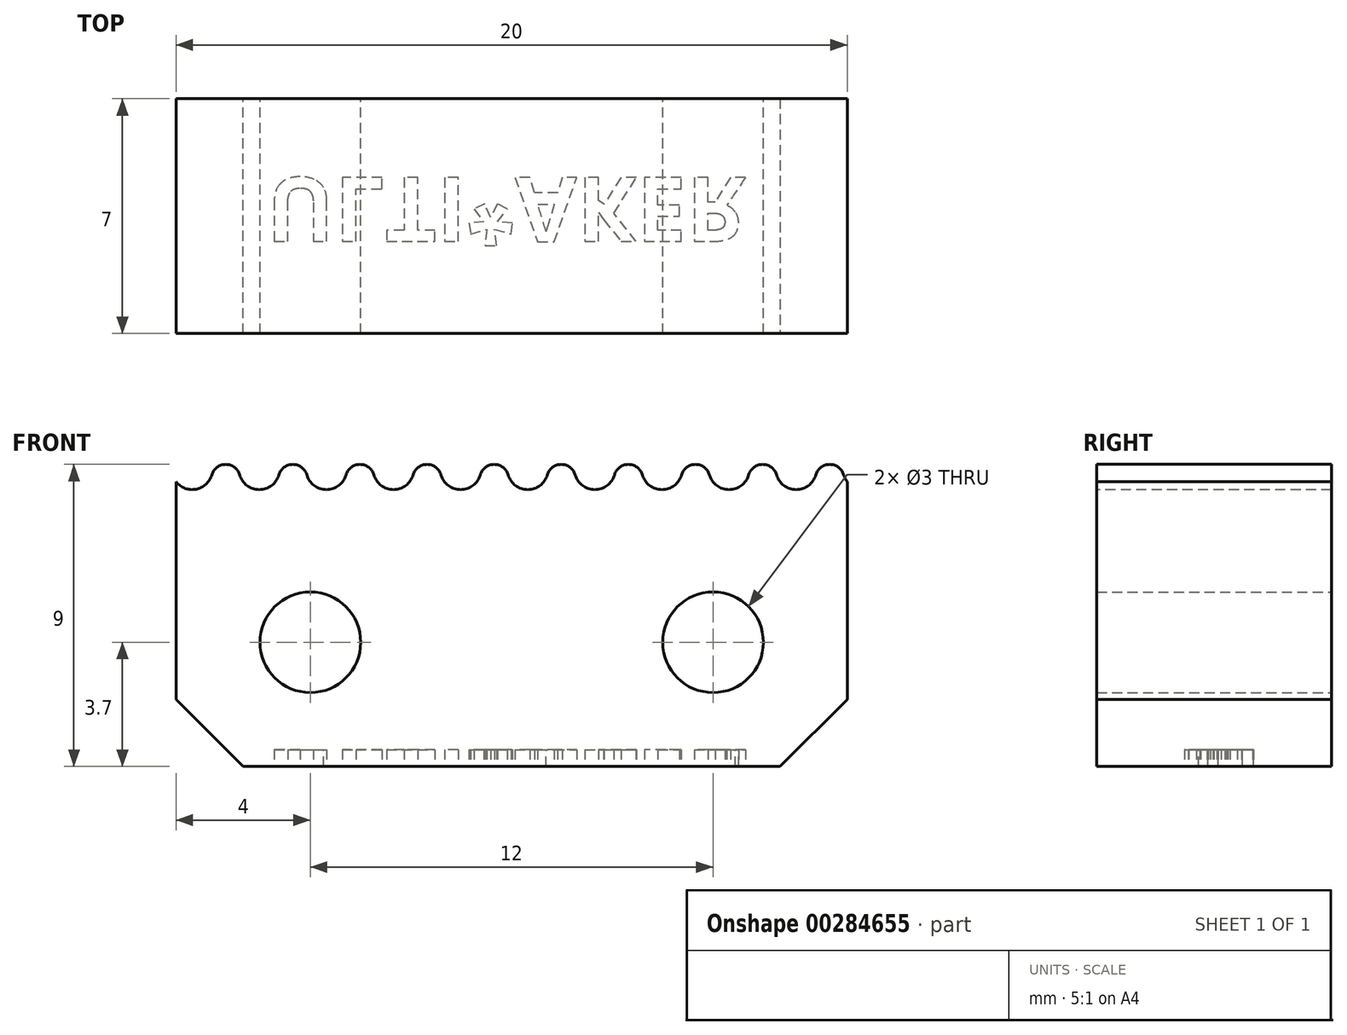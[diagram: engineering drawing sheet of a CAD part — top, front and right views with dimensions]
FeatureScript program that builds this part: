
annotation { "Feature Type Name" : "Feature", "Feature Type Description" : "" }
export const myFeature = defineFeature(function(context is Context, id is Id, definition is map)
    precondition{}
    {
        {
            var Q0;
            Q0=qCreatedBy(makeId("Front.planeOp"),FACE);
            var sketch = newSketch(context, id + "F0", { "sketchPlane" : qUnion([Q0])});
            skLineSegment(sketch, "E0.bottom", {"start": v(2, 1) * mm, "end": v(22, 1) * mm});
            skLineSegment(sketch, "E0.top", {"start": v(2, 10) * mm, "end": v(22, 10) * mm});
            skLineSegment(sketch, "E0.left", {"start": v(2, 1) * mm, "end": v(2, 10) * mm});
            skLineSegment(sketch, "E0.right", {"start": v(22, 1) * mm, "end": v(22, 10) * mm});
            skCircle(sketch, "E1", {"center": v(6, 4.7) * mm, "radius": 1.5 * mm});
            skPoint(sketch, "E1.centerSnap0", {"position": v(2, 4.7) * mm});
            skCircle(sketch, "E2", {"center": v(18, 4.7) * mm, "radius": 1.5 * mm});
            skPoint(sketch, "E2.centerSnap0", {"position": v(22, 4.7) * mm});
            skSolve(sketch);
        }
        {
            var Q0;
            Q0=makeQuery(id+"F0.imprint","IMPRINT",FACE,{"disambiguationData":[TD([[makeQuery(id+"F0.imprint","IMPRINT",EDGE,{"derivedFrom":sQuery(id+"F0.wireOp",EDGE,"E0.bottom")}),1.0]])]});
            extrude(context, id + "F1", {"entities" : qUnion([Q0]), "depth" : 7 * mm});
        }
        {
            var Q0;
            Q0=makeQuery(id+"F1.opExtrude","CAP_FACE",FACE,{"disambiguationData":[OSD([sQuery(id+"F0.wireOp",EDGE,"E0.bottom"),sQuery(id+"F0.wireOp",EDGE,"E0.top"),sQuery(id+"F0.wireOp",EDGE,"E0.left"),sQuery(id+"F0.wireOp",EDGE,"E0.right"),sQuery(id+"F0.wireOp",EDGE,"E1"),sQuery(id+"F0.wireOp",EDGE,"E2")])],"isStart":false});
            var sketch = newSketch(context, id + "F2", { "sketchPlane" : qUnion([Q0])});
            skLineSegment(sketch, "E3.top", {"start": v(0, 10.63) * mm, "end": v(22.94, 10.63) * mm});
            skArc(sketch, "E4", {"start": v(2.48, 9.25) * mm, "mid": v(2.84, 9.37) * mm, "end": v(3.06, 9.69) * mm});
            skArc(sketch, "E5", {"start": v(3.9, 9.69) * mm, "mid": v(4.11, 9.37) * mm, "end": v(4.48, 9.25) * mm});
            skArc(sketch, "E6", {"start": v(3.9, 9.69) * mm, "mid": v(3.48, 10) * mm, "end": v(3.06, 9.69) * mm});
            skPoint(sketch, "E6.first.point", {"position": v(3.48, 10) * mm});
            skPoint(sketch, "E6.second.point", {"position": v(3.06, 9.69) * mm});
            skPoint(sketch, "E6.third.point", {"position": v(3.9, 9.69) * mm});
            skLineSegment(sketch, "E7.trimOffspring", {"start": v(3.48, 10) * mm, "end": v(3.48, 10) * mm});
            skLineSegment(sketch, "E8", {"start": v(4.48, 10.86) * mm, "end": v(4.48, 10.63) * mm});
            skPoint(sketch, "E9.start.orphan", {"position": v(2.48, 10.63) * mm});
            skArc(sketch, "E10.1.0.0", {"start": v(5.9, 9.69) * mm, "mid": v(6.11, 9.37) * mm, "end": v(6.48, 9.25) * mm});
            skPoint(sketch, "E10.1.0.1", {"position": v(5.06, 9.69) * mm});
            skArc(sketch, "E10.1.0.2", {"start": v(4.48, 9.25) * mm, "mid": v(4.84, 9.37) * mm, "end": v(5.06, 9.69) * mm});
            skArc(sketch, "E10.1.0.3", {"start": v(5.9, 9.69) * mm, "mid": v(5.48, 10) * mm, "end": v(5.06, 9.69) * mm});
            skArc(sketch, "E10.2.0.0", {"start": v(7.9, 9.69) * mm, "mid": v(8.11, 9.37) * mm, "end": v(8.48, 9.25) * mm});
            skPoint(sketch, "E10.2.0.1", {"position": v(7.06, 9.69) * mm});
            skArc(sketch, "E10.2.0.2", {"start": v(6.48, 9.25) * mm, "mid": v(6.84, 9.37) * mm, "end": v(7.06, 9.69) * mm});
            skArc(sketch, "E10.2.0.3", {"start": v(7.9, 9.69) * mm, "mid": v(7.48, 10) * mm, "end": v(7.06, 9.69) * mm});
            skArc(sketch, "E10.3.0.0", {"start": v(9.9, 9.69) * mm, "mid": v(10.11, 9.37) * mm, "end": v(10.48, 9.25) * mm});
            skPoint(sketch, "E10.3.0.1", {"position": v(9.06, 9.69) * mm});
            skArc(sketch, "E10.3.0.2", {"start": v(8.48, 9.25) * mm, "mid": v(8.84, 9.37) * mm, "end": v(9.06, 9.69) * mm});
            skArc(sketch, "E10.3.0.3", {"start": v(9.9, 9.69) * mm, "mid": v(9.48, 10) * mm, "end": v(9.06, 9.69) * mm});
            skArc(sketch, "E10.4.0.0", {"start": v(11.9, 9.69) * mm, "mid": v(12.11, 9.37) * mm, "end": v(12.48, 9.25) * mm});
            skPoint(sketch, "E10.4.0.1", {"position": v(11.06, 9.69) * mm});
            skArc(sketch, "E10.4.0.2", {"start": v(10.48, 9.25) * mm, "mid": v(10.84, 9.37) * mm, "end": v(11.06, 9.69) * mm});
            skArc(sketch, "E10.4.0.3", {"start": v(11.9, 9.69) * mm, "mid": v(11.48, 10) * mm, "end": v(11.06, 9.69) * mm});
            skArc(sketch, "E10.5.0.0", {"start": v(13.9, 9.69) * mm, "mid": v(14.11, 9.37) * mm, "end": v(14.48, 9.25) * mm});
            skPoint(sketch, "E10.5.0.1", {"position": v(13.06, 9.69) * mm});
            skArc(sketch, "E10.5.0.2", {"start": v(12.48, 9.25) * mm, "mid": v(12.84, 9.37) * mm, "end": v(13.06, 9.69) * mm});
            skArc(sketch, "E10.5.0.3", {"start": v(13.9, 9.69) * mm, "mid": v(13.48, 10) * mm, "end": v(13.06, 9.69) * mm});
            skArc(sketch, "E10.6.0.0", {"start": v(15.9, 9.69) * mm, "mid": v(16.11, 9.37) * mm, "end": v(16.48, 9.25) * mm});
            skPoint(sketch, "E10.6.0.1", {"position": v(15.06, 9.69) * mm});
            skArc(sketch, "E10.6.0.2", {"start": v(14.48, 9.25) * mm, "mid": v(14.84, 9.37) * mm, "end": v(15.06, 9.69) * mm});
            skArc(sketch, "E10.6.0.3", {"start": v(15.9, 9.69) * mm, "mid": v(15.48, 10) * mm, "end": v(15.06, 9.69) * mm});
            skArc(sketch, "E10.7.0.0", {"start": v(17.9, 9.69) * mm, "mid": v(18.11, 9.37) * mm, "end": v(18.48, 9.25) * mm});
            skPoint(sketch, "E10.7.0.1", {"position": v(17.06, 9.69) * mm});
            skArc(sketch, "E10.7.0.2", {"start": v(16.48, 9.25) * mm, "mid": v(16.84, 9.37) * mm, "end": v(17.06, 9.69) * mm});
            skArc(sketch, "E10.7.0.3", {"start": v(17.9, 9.69) * mm, "mid": v(17.48, 10) * mm, "end": v(17.06, 9.69) * mm});
            skArc(sketch, "E10.8.0.0", {"start": v(19.9, 9.69) * mm, "mid": v(20.11, 9.37) * mm, "end": v(20.48, 9.25) * mm});
            skPoint(sketch, "E10.8.0.1", {"position": v(19.06, 9.69) * mm});
            skArc(sketch, "E10.8.0.2", {"start": v(18.48, 9.25) * mm, "mid": v(18.84, 9.37) * mm, "end": v(19.06, 9.69) * mm});
            skArc(sketch, "E10.8.0.3", {"start": v(19.9, 9.69) * mm, "mid": v(19.48, 10) * mm, "end": v(19.06, 9.69) * mm});
            skArc(sketch, "E10.9.0.0", {"start": v(21.9, 9.69) * mm, "mid": v(22.11, 9.37) * mm, "end": v(22.48, 9.25) * mm});
            skPoint(sketch, "E10.9.0.1", {"position": v(21.06, 9.69) * mm});
            skArc(sketch, "E10.9.0.2", {"start": v(20.48, 9.25) * mm, "mid": v(20.84, 9.37) * mm, "end": v(21.06, 9.69) * mm});
            skArc(sketch, "E10.9.0.3", {"start": v(21.9, 9.69) * mm, "mid": v(21.48, 10) * mm, "end": v(21.06, 9.69) * mm});
            skArc(sketch, "E10.10.0.0", {"start": v(23.9, 9.69) * mm, "mid": v(24.11, 9.37) * mm, "end": v(24.48, 9.25) * mm});
            skPoint(sketch, "E10.10.0.1", {"position": v(23.06, 9.69) * mm});
            skArc(sketch, "E10.10.0.2", {"start": v(22.48, 9.25) * mm, "mid": v(22.84, 9.37) * mm, "end": v(23.06, 9.69) * mm});
            skArc(sketch, "E10.10.0.3", {"start": v(23.9, 9.69) * mm, "mid": v(23.48, 10) * mm, "end": v(23.06, 9.69) * mm});
            skPoint(sketch, "E10.11.0.1", {"position": v(25.06, 9.69) * mm});
            skArc(sketch, "E11.1.0.0", {"start": v(0.48, 9.25) * mm, "mid": v(0.84, 9.37) * mm, "end": v(1.06, 9.69) * mm});
            skArc(sketch, "E11.1.0.1", {"start": v(1.9, 9.69) * mm, "mid": v(1.48, 10) * mm, "end": v(1.06, 9.69) * mm});
            skArc(sketch, "E11.1.0.2", {"start": v(1.9, 9.69) * mm, "mid": v(2.11, 9.37) * mm, "end": v(2.48, 9.25) * mm});
            skArc(sketch, "E11.2.0.0", {"start": v(-1.52, 9.25) * mm, "mid": v(-1.16, 9.37) * mm, "end": v(-0.94, 9.69) * mm});
            skArc(sketch, "E11.2.0.1", {"start": v(-0.1, 9.69) * mm, "mid": v(-0.52, 10) * mm, "end": v(-0.94, 9.69) * mm});
            skArc(sketch, "E11.2.0.2", {"start": v(-0.1, 9.69) * mm, "mid": v(0.11, 9.37) * mm, "end": v(0.48, 9.25) * mm});
            skLineSegment(sketch, "E11.direction1", {"start": v(2.48, 9.25) * mm, "end": v(0.48, 9.25) * mm, "construction": true});
            skLineSegment(sketch, "E12", {"start": v(0, 10.63) * mm, "end": v(-1.66, 10.63) * mm});
            skLineSegment(sketch, "E13", {"start": v(-1.66, 10.63) * mm, "end": v(-1.52, 9.25) * mm});
            skLineSegment(sketch, "E14", {"start": v(22.94, 10.63) * mm, "end": v(24.4, 10.63) * mm});
            skLineSegment(sketch, "E15", {"start": v(24.4, 10.63) * mm, "end": v(24.48, 9.25) * mm});
            skSolve(sketch);
        }
        {
            var Q0;
            Q0=makeQuery(id+"F2.imprint","IMPRINT",FACE,{"disambiguationData":[TD([[makeQuery(id+"F2.imprint","IMPRINT",EDGE,{"derivedFrom":sQuery(id+"F2.wireOp",EDGE,"E11.2.0.0")}),1.0]])]});
            var Q1;
            {var subQ1=sQuery(id+"F2.wireOp",EDGE,"E11.1.0.0");Q1=makeQuery(id+"F2.imprint","IMPRINT",FACE,{"disambiguationData":[TD([[makeQuery(id+"F2.imprint","IMPRINT",EDGE,{"derivedFrom":subQ1}),1.0]])]});}
            var Q2;
            {var subQ5=sQuery(id+"F2.wireOp",EDGE,"E4");Q2=makeQuery(id+"F2.imprint","IMPRINT",FACE,{"disambiguationData":[TD([[makeQuery(id+"F2.imprint","IMPRINT",EDGE,{"derivedFrom":subQ5}),1.0]])]});}
            var Q3;
            {var subQ5=sQuery(id+"F2.wireOp",EDGE,"E5");Q3=makeQuery(id+"F2.imprint","IMPRINT",FACE,{"disambiguationData":[TD([[makeQuery(id+"F2.imprint","IMPRINT",EDGE,{"derivedFrom":subQ5}),1.0]])]});}
            var Q4;
            {var subQ5=sQuery(id+"F2.wireOp",EDGE,"E10.1.0.0");Q4=makeQuery(id+"F2.imprint","IMPRINT",FACE,{"disambiguationData":[TD([[makeQuery(id+"F2.imprint","IMPRINT",EDGE,{"derivedFrom":subQ5}),1.0]])]});}
            var Q5;
            {var subQ5=sQuery(id+"F2.wireOp",EDGE,"E10.2.0.0");Q5=makeQuery(id+"F2.imprint","IMPRINT",FACE,{"disambiguationData":[TD([[makeQuery(id+"F2.imprint","IMPRINT",EDGE,{"derivedFrom":subQ5}),1.0]])]});}
            var Q6;
            {var subQ5=sQuery(id+"F2.wireOp",EDGE,"E10.3.0.0");Q6=makeQuery(id+"F2.imprint","IMPRINT",FACE,{"disambiguationData":[TD([[makeQuery(id+"F2.imprint","IMPRINT",EDGE,{"derivedFrom":subQ5}),1.0]])]});}
            var Q7;
            {var subQ5=sQuery(id+"F2.wireOp",EDGE,"E10.4.0.0");Q7=makeQuery(id+"F2.imprint","IMPRINT",FACE,{"disambiguationData":[TD([[makeQuery(id+"F2.imprint","IMPRINT",EDGE,{"derivedFrom":subQ5}),1.0]])]});}
            var Q8;
            {var subQ5=sQuery(id+"F2.wireOp",EDGE,"E10.5.0.0");Q8=makeQuery(id+"F2.imprint","IMPRINT",FACE,{"disambiguationData":[TD([[makeQuery(id+"F2.imprint","IMPRINT",EDGE,{"derivedFrom":subQ5}),1.0]])]});}
            var Q9;
            {var subQ5=sQuery(id+"F2.wireOp",EDGE,"E10.6.0.0");Q9=makeQuery(id+"F2.imprint","IMPRINT",FACE,{"disambiguationData":[TD([[makeQuery(id+"F2.imprint","IMPRINT",EDGE,{"derivedFrom":subQ5}),1.0]])]});}
            var Q10;
            {var subQ5=sQuery(id+"F2.wireOp",EDGE,"E10.7.0.0");Q10=makeQuery(id+"F2.imprint","IMPRINT",FACE,{"disambiguationData":[TD([[makeQuery(id+"F2.imprint","IMPRINT",EDGE,{"derivedFrom":subQ5}),1.0]])]});}
            var Q11;
            {var subQ5=sQuery(id+"F2.wireOp",EDGE,"E10.8.0.0");Q11=makeQuery(id+"F2.imprint","IMPRINT",FACE,{"disambiguationData":[TD([[makeQuery(id+"F2.imprint","IMPRINT",EDGE,{"derivedFrom":subQ5}),1.0]])]});}
            var Q12;
            {var subQ5=sQuery(id+"F2.wireOp",EDGE,"E10.9.0.0");Q12=makeQuery(id+"F2.imprint","IMPRINT",FACE,{"disambiguationData":[TD([[makeQuery(id+"F2.imprint","IMPRINT",EDGE,{"derivedFrom":subQ5}),1.0]])]});}
            var Q13;
            {var subQ0=sQuery(id+"F2.wireOp",EDGE,"E10.10.0.3");var subQ1=sQuery(id+"F2.wireOp",EDGE,"E10.10.0.0");var subQ2=makeQuery(id+"F2.imprint","INTERSECT",VERTEX,{"derivedFrom":[subQ1,subQ0]});Q13=makeQuery(id+"F2.imprint","IMPRINT",FACE,{"disambiguationData":[TD([[makeQuery(id+"F2.imprint","IMPRINT",EDGE,{"disambiguationData":[TD([[subQ2,-1.0]])],"derivedFrom":subQ1}),1.0]])]});}
            extrude(context, id + "F3", {"entities" : qUnion([Q0, Q1, Q2, Q3, Q4, Q5, Q6, Q7, Q8, Q9, Q10, Q11, Q12, Q13]), "operationType" : NewBodyOperationType.REMOVE, "oppositeDirection" : true, "depth" : 25 * mm});
        }
        {
            var Q0;
            Q0=makeQuery(id+"F1.opExtrude","SWEPT_EDGE",EDGE,{"disambiguationData":[OSD([sQuery(id+"F0.wireOp",EDGE,"E0.bottom"),sQuery(id+"F0.wireOp",EDGE,"E0.left")])]});
            var Q1;
            Q1=makeQuery(id+"F1.opExtrude","SWEPT_EDGE",EDGE,{"disambiguationData":[OSD([sQuery(id+"F0.wireOp",EDGE,"E0.bottom"),sQuery(id+"F0.wireOp",EDGE,"E0.right")])]});
            chamfer(context, id + "F4", {"entities" : qUnion([Q0, Q1]), "width" : 2 * mm, "tangentPropagation" : true});
        }
        {
            var Q0;
            Q0=makeQuery(id+"F1.opExtrude","SWEPT_FACE",FACE,{"disambiguationData":[OSD([sQuery(id+"F0.wireOp",EDGE,"E0.bottom")])]});
            var sketch = newSketch(context, id + "F5", { "sketchPlane" : qUnion([Q0])});
            skText(sketch, "E16", { "text": "ULTI*AKER", "fontName": "OpenSans-Bold.ttf"});
            const initialGuessF5  = {"E16": [0.0047, 0.00235, 1, 0, 0.00192]};
            skSetInitialGuess(sketch, initialGuessF5);
            skSolve(sketch);
        }
        {
            var Q0;
            Q0 = qSketchRegion(id + "F5", true);
            extrude(context, id + "F6", {"entities" : qUnion([Q0]), "operationType" : NewBodyOperationType.REMOVE, "oppositeDirection" : true, "depth" : 0.5 * mm});
        }
    });
